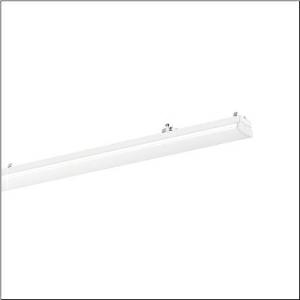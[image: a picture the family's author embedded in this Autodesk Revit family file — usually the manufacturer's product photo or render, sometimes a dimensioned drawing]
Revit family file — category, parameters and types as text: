
# Revit family: licross_r__21_recessed_opal_mo_52tl1ddn495g_bbb7
name_source: partatom
category: Lighting Fixtures
units: mm (PartAtom-declared; Revit-internal decimal feet)

## family parameters
Cut with Voids When Loaded = No
Host = Face
Light Source = No
Part Type = Normal
Room Calculation Point = No
Round Connector Dimension = Use Diameter
Shared = No

## types (1)
- --- (1 x LED, 9740 lm, 58 W, 4000K)
    Apparent Load = 58 VA
    CIE Flux Codes = 44 73 91 87 100
    Color Rendering = 80
    Color Temperature = 4000K
    Default Elevation = 1800 mm
    Description = Licross® 21 recessed opal MO, luminaire insert, of sheet steel, galvanised, coil coated, white, length: 1.500mm, width: 66mm, height: 67mm, LED rated luminous flux: 9.750lm, light colour: 840, control gear: DALI 2, with plug, 5-pole, with phase selection, mains connection: 220..240V, AC, 50/60Hz, rated input power: 58W, internal wiring halogen-free, primary optical cover: cover, of PMMA, light emission: direct with ceiling illumination distribution, primary light characteristic: symmetric, protection rating (complete): IP40, insulation class (complete): insulation class I (protective earthing), certification: CE, ENEC, VDE, UKCA, protection symbol: D if used in an environment without relevant dust loads with corresponding accessories, impact resistance: IK06, permissible ambient temperature for indoor applications: -25..+35°C, corresponds to IFS (International Featured Standards) requirements for safety and quality in the food industry, reducing of maximum allowable ambient temperature of 5°C with ceiling mounting, LABS conformity tested according to VDMA 24364:2018-05, packaging unit: 1 piece
    Height = 83 mm
    Lamp = 1 x LED
    Lamp Light Flux = 9740 lm
    Lamp Power = 58 W
    Lamp count = 1
    Length = 1500 mm
    Luminous efficacy = 168 lm/W
    Manufacturer = Siteco
    ModVariant = No
    Model = 52TL1DDN495G
    Mounting Place = Ceiling
    Mounting Type = Pendant
    Number of Poles = 1
    OnlyDefault = Yes
    Power Factor = 1
    Product Name = Licross® 21 recessed opal MO
    Product group = luminaire insert | ceiling pendant
    ProductGroupID = 902
    Protection Class = Protection class I
    Protection Degree = IP 40
    RLX_Detail_Level = 1
    RLX_Emergency_Light_Flux = 0 lm
    RLX_Emergency_Type = 0
    RLX_Emergency_Type_DB = No
    RlxData = <blob elided: 26849 chars, md5=0767d583>
    Socket = socket
    Standby Power = 0 W
    System Light Flux = 9740 lm
    System Power = 58 W
    Type Comments = factory setting: luminous flux: 100 % | dim-lin: 254 | 390 mA
    Type Image = l_1313666.jpg
    URL = http://relux.com
    VarID = @adj_090111
    Voltage = 0 V
    Weight = 0.00 kg
    Width = 76 mm

## geometry (parser evidence)
native form markers: Blend x4, Sweep x13
no freeform markers — native parametric forms only
